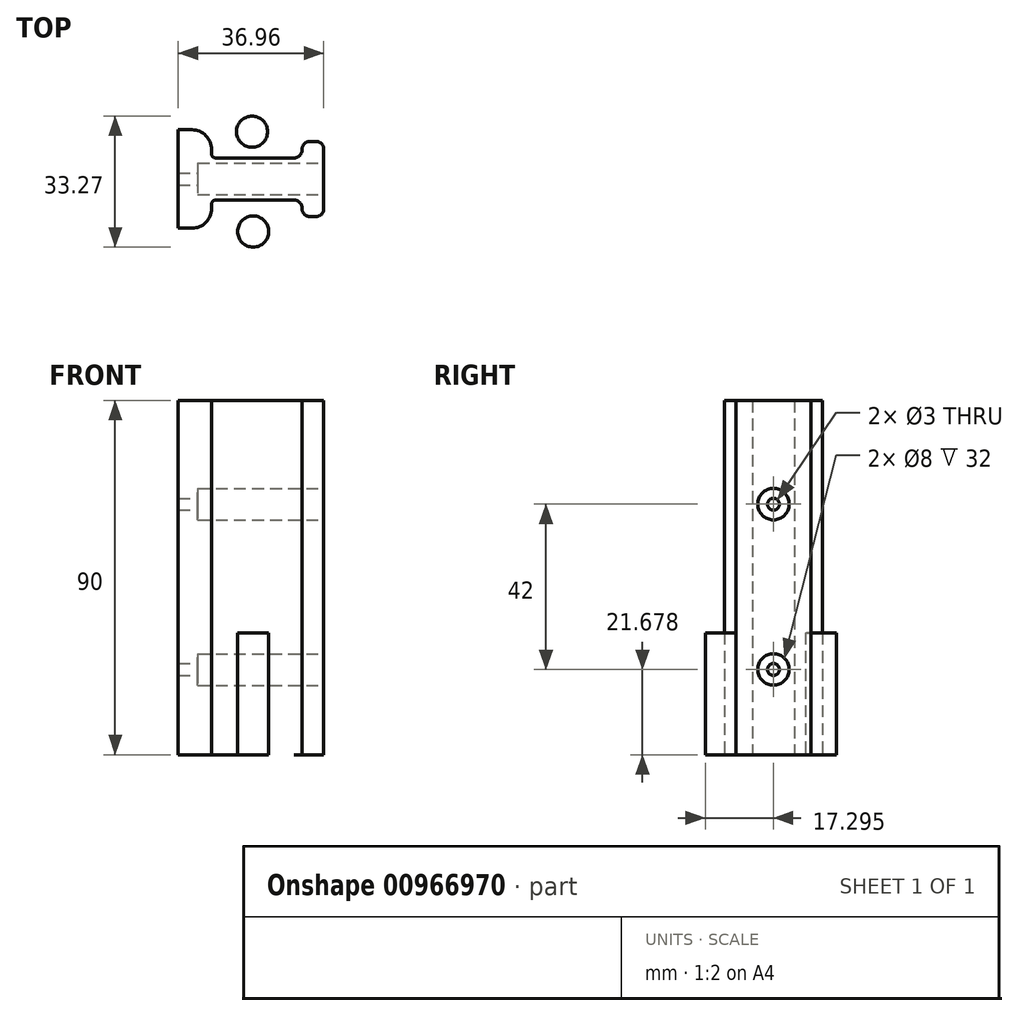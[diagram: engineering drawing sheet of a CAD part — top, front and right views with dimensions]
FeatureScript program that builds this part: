
annotation { "Feature Type Name" : "Feature", "Feature Type Description" : "" }
export const myFeature = defineFeature(function(context is Context, id is Id, definition is map)
    precondition{}
    {
        {
            var Q0;
            Q0=qCreatedBy(makeId("Top.planeOp"),FACE);
            var sketch = newSketch(context, id + "F0", { "sketchPlane" : qUnion([Q0])});
            skLineSegment(sketch, "E0", {"start": v(-32.17, 16.22) * mm, "end": v(-32.17, 16.22) * mm});
            skPoint(sketch, "E1.orphan", {"position": v(-32.17, -8.78) * mm});
            skLineSegment(sketch, "E2", {"start": v(-32.17, -8.78) * mm, "end": v(-32.17, 16.22) * mm});
            skLineSegment(sketch, "E3", {"start": v(-32.17, 16.22) * mm, "end": v(-28.7, 16.22) * mm});
            skLineSegment(sketch, "E4", {"start": v(-22.7, 9.08) * mm, "end": v(-2.7, 9.08) * mm});
            skLineSegment(sketch, "E5", {"start": v(-0.7, 11.08) * mm, "end": v(-0.7, 11.28) * mm});
            skLineSegment(sketch, "E6", {"start": v(1.3, 13.28) * mm, "end": v(2.79, 13.28) * mm});
            skLineSegment(sketch, "E7", {"start": v(4.79, 11.28) * mm, "end": v(4.79, 3.72) * mm});
            skPoint(sketch, "E8.visualSharp", {"position": v(-23.7, 16.22) * mm});
            skLineSegment(sketch, "E8.filletArc", {"start": v(-23.7, 16.22) * mm, "end": v(-23.7, 16.22) * mm});
            skArc(sketch, "E9.filletArc", {"start": v(-23.7, 11.22) * mm, "mid": v(-25.17, 14.75) * mm, "end": v(-28.7, 16.22) * mm});
            skLineSegment(sketch, "E10", {"start": v(-23.7, 10.08) * mm, "end": v(-23.7, 11.22) * mm});
            skPoint(sketch, "E11.visualSharp", {"position": v(-23.7, 9.08) * mm});
            skArc(sketch, "E11.filletArc", {"start": v(-23.7, 10.08) * mm, "mid": v(-23.41, 9.37) * mm, "end": v(-22.7, 9.08) * mm});
            skPoint(sketch, "E12.visualSharp", {"position": v(-0.7, 9.08) * mm});
            skArc(sketch, "E12.filletArc", {"start": v(-2.7, 9.08) * mm, "mid": v(-1.29, 9.66) * mm, "end": v(-0.7, 11.08) * mm});
            skPoint(sketch, "E13.visualSharp", {"position": v(-0.7, 13.28) * mm});
            skArc(sketch, "E13.filletArc", {"start": v(1.3, 13.28) * mm, "mid": v(-0.12, 12.7) * mm, "end": v(-0.7, 11.28) * mm});
            skPoint(sketch, "E14.visualSharp", {"position": v(4.79, 13.28) * mm});
            skArc(sketch, "E14.filletArc", {"start": v(4.79, 11.28) * mm, "mid": v(4.2, 12.7) * mm, "end": v(2.79, 13.28) * mm});
            skLineSegment(sketch, "E15.MirrorCS", {"start": v(-0.7, -3.65) * mm, "end": v(-0.7, -3.85) * mm});
            skPoint(sketch, "E16.MirrorP", {"position": v(-23.7, -8.78) * mm});
            skLineSegment(sketch, "E17.MirrorCS", {"start": v(1.3, -5.85) * mm, "end": v(2.79, -5.85) * mm});
            skArc(sketch, "E18.MirrorCS", {"start": v(1.3, -5.85) * mm, "mid": v(-0.12, -5.26) * mm, "end": v(-0.7, -3.85) * mm});
            skPoint(sketch, "E19.MirrorP", {"position": v(-23.7, -1.65) * mm});
            skLineSegment(sketch, "E20.MirrorCS", {"start": v(-23.7, -2.65) * mm, "end": v(-23.7, -3.78) * mm});
            skLineSegment(sketch, "E21.MirrorCS", {"start": v(-22.7, -1.65) * mm, "end": v(-2.7, -1.65) * mm});
            skArc(sketch, "E22.MirrorCS", {"start": v(4.79, -3.85) * mm, "mid": v(4.2, -5.26) * mm, "end": v(2.79, -5.85) * mm});
            skPoint(sketch, "E23.MirrorP", {"position": v(4.79, -5.85) * mm});
            skLineSegment(sketch, "E24.MirrorCS", {"start": v(4.79, -3.85) * mm, "end": v(4.79, 3.72) * mm});
            skPoint(sketch, "E25.MirrorP", {"position": v(-0.7, -1.65) * mm});
            skArc(sketch, "E26.MirrorCS", {"start": v(-23.7, -2.65) * mm, "mid": v(-23.41, -1.94) * mm, "end": v(-22.7, -1.65) * mm});
            skArc(sketch, "E27.MirrorCS", {"start": v(-23.7, -3.78) * mm, "mid": v(-25.17, -7.32) * mm, "end": v(-28.7, -8.78) * mm});
            skLineSegment(sketch, "E28.MirrorCS", {"start": v(-23.7, -8.78) * mm, "end": v(-23.7, -8.78) * mm});
            skArc(sketch, "E29.MirrorCS", {"start": v(-2.7, -1.65) * mm, "mid": v(-1.29, -2.23) * mm, "end": v(-0.7, -3.65) * mm});
            skPoint(sketch, "E30.MirrorP", {"position": v(-0.7, -5.85) * mm});
            skLineSegment(sketch, "E31", {"start": v(-32.17, -8.78) * mm, "end": v(-28.7, -8.78) * mm});
            skSolve(sketch);
        }
        {
            var Q0;
            Q0 = qSketchRegion(id + "F0", true);
            extrude(context, id + "F1", {"entities" : qUnion([Q0]), "depth" : 90 * mm, "offsetDistance" : 25 * mm});
        }
        {
            var Q0;
            Q0 = qSketchRegion(id + "F0", true);
            extrude(context, id + "F2", {"entities" : qUnion([Q0]), "operationType" : NewBodyOperationType.ADD, "depth" : 90 * mm, "offsetDistance" : 25 * mm});
        }
        {
            var Q0;
            Q0=makeQuery(id+"F1.opExtrude","SWEPT_FACE",FACE,{"disambiguationData":[OSD([sQuery(id+"F0.wireOp",EDGE,"E7"),sQuery(id+"F0.wireOp",EDGE,"E24.MirrorCS")])]});
            var sketch = newSketch(context, id + "F3", { "sketchPlane" : qUnion([Q0])});
            skCircle(sketch, "E32", {"center": v(3.72, 63.68) * mm, "radius": 4 * mm});
            skCircle(sketch, "E33", {"center": v(3.72, 21.68) * mm, "radius": 4 * mm});
            skCircle(sketch, "E34", {"center": v(3.72, 63.68) * mm, "radius": 1.5 * mm});
            skCircle(sketch, "E35", {"center": v(3.72, 21.68) * mm, "radius": 1.5 * mm});
            skSolve(sketch);
        }
        {
            var Q0;
            Q0=makeQuery(id+"F3.imprint","IMPRINT",FACE,{"disambiguationData":[TD([[makeQuery(id+"F3.imprint","IMPRINT",EDGE,{"derivedFrom":sQuery(id+"F3.wireOp",EDGE,"E34")}),1.0]])]});
            var Q1;
            Q1=makeQuery(id+"F3.imprint","IMPRINT",FACE,{"disambiguationData":[TD([[makeQuery(id+"F3.imprint","IMPRINT",EDGE,{"derivedFrom":sQuery(id+"F3.wireOp",EDGE,"E35")}),1.0]])]});
            var Q2;
            Q2 = qConstructionFilter(qBodyType(qCreatedBy(id + "F3" ,EDGE), BodyType.WIRE), ConstructionObject.NO);
            extrude(context, id + "F4", {"entities" : qUnion([Q0, Q1]), "operationType" : NewBodyOperationType.REMOVE, "surfaceEntities" : qUnion([Q2]), "oppositeDirection" : true, "depth" : 54 * mm, "offsetDistance" : 25 * mm});
        }
        {
            var Q0;
            Q0 = qSketchRegion(id + "F3", true);
            var Q1;
            Q1 = qConstructionFilter(qBodyType(qCreatedBy(id + "F3" ,EDGE), BodyType.WIRE), ConstructionObject.NO);
            extrude(context, id + "F5", {"entities" : qUnion([Q0]), "operationType" : NewBodyOperationType.REMOVE, "surfaceEntities" : qUnion([Q1]), "oppositeDirection" : true, "depth" : 32 * mm, "offsetDistance" : 25 * mm});
        }
        {
            var Q0;
            Q0=qCreatedBy(makeId("Top.planeOp"),FACE);
            var sketch = newSketch(context, id + "F6", { "sketchPlane" : qUnion([Q0])});
            skCircle(sketch, "E36", {"center": v(-13.42, 15.74) * mm, "radius": 3.95 * mm});
            skCircle(sketch, "E37", {"center": v(-13.13, -9.63) * mm, "radius": 3.95 * mm});
            skSolve(sketch);
        }
        {
            var Q0;
            Q0 = qSketchRegion(id + "F6", true);
            extrude(context, id + "F7", {"entities" : qUnion([Q0]), "depth" : 31 * mm, "offsetDistance" : 25 * mm});
        }
    });
